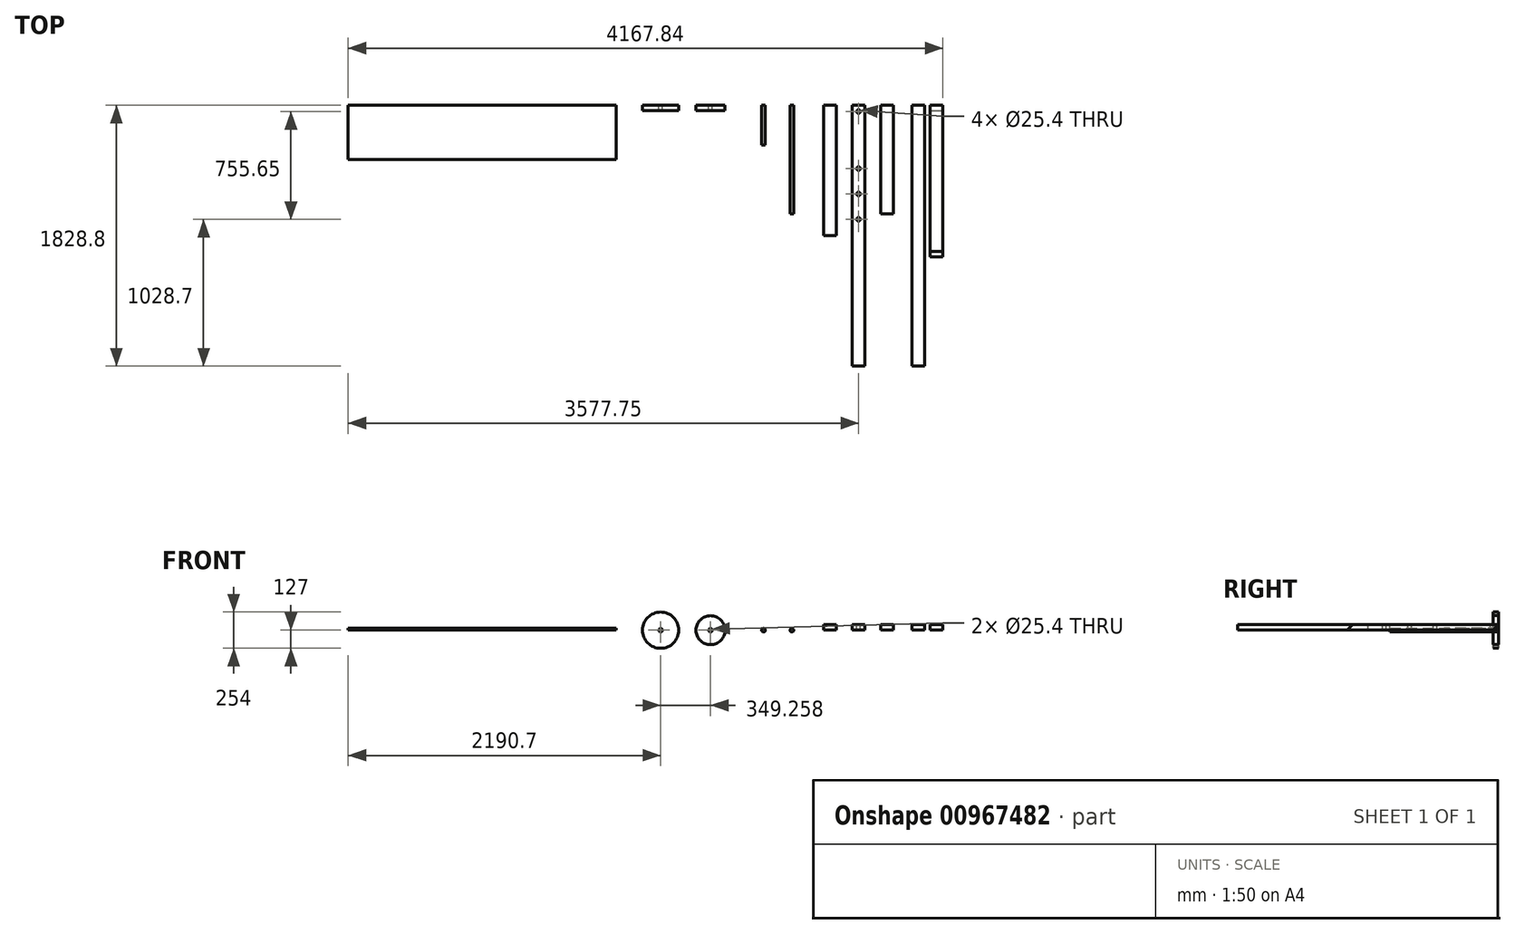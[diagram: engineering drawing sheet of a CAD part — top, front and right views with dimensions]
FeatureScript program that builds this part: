
annotation { "Feature Type Name" : "Feature", "Feature Type Description" : "" }
export const myFeature = defineFeature(function(context is Context, id is Id, definition is map)
    precondition{}
    {
        {
            var Q0;
            Q0=qCreatedBy(makeId("Front.planeOp"),FACE);
            var sketch = newSketch(context, id + "F0", { "sketchPlane" : qUnion([Q0])});
            skLineSegment(sketch, "E0.bottom", {"start": v(200.4, 0) * mm, "end": v(289.3, 0) * mm});
            skLineSegment(sketch, "E0.top", {"start": v(200.4, 38.1) * mm, "end": v(289.3, 38.1) * mm});
            skLineSegment(sketch, "E0.left", {"start": v(200.4, 0) * mm, "end": v(200.4, 38.1) * mm});
            skLineSegment(sketch, "E0.right", {"start": v(289.3, 0) * mm, "end": v(289.3, 38.1) * mm});
            skLineSegment(sketch, "E1.bottom", {"start": v(399.3, 0) * mm, "end": v(488.2, 0) * mm});
            skLineSegment(sketch, "E1.top", {"start": v(399.3, 38.1) * mm, "end": v(488.2, 38.1) * mm});
            skLineSegment(sketch, "E1.left", {"start": v(399.3, 0) * mm, "end": v(399.3, 38.1) * mm});
            skLineSegment(sketch, "E1.right", {"start": v(488.2, 0) * mm, "end": v(488.2, 38.1) * mm});
            skLineSegment(sketch, "E2.bottom", {"start": v(619.29, 0) * mm, "end": v(708.19, 0) * mm});
            skLineSegment(sketch, "E2.top", {"start": v(619.29, 38.1) * mm, "end": v(708.19, 38.1) * mm});
            skLineSegment(sketch, "E2.left", {"start": v(619.29, 0) * mm, "end": v(619.29, 38.1) * mm});
            skLineSegment(sketch, "E2.right", {"start": v(708.19, 0) * mm, "end": v(708.19, 38.1) * mm});
            skLineSegment(sketch, "E3.bottom", {"start": v(0, 0) * mm, "end": v(88.9, 0) * mm});
            skLineSegment(sketch, "E3.top", {"start": v(0, 38.1) * mm, "end": v(88.9, 38.1) * mm});
            skLineSegment(sketch, "E3.left", {"start": v(0, 0) * mm, "end": v(0, 38.1) * mm});
            skLineSegment(sketch, "E3.right", {"start": v(88.9, 0) * mm, "end": v(88.9, 38.1) * mm});
            skSolve(sketch);
        }
        {
            var Q0;
            Q0=makeQuery(id+"F0.imprint","IMPRINT",FACE,{"disambiguationData":[TD([[makeQuery(id+"F0.imprint","IMPRINT",EDGE,{"derivedFrom":sQuery(id+"F0.wireOp",EDGE,"E3.bottom")}),1.0]])]});
            extrude(context, id + "F1", {"entities" : qUnion([Q0]), "depth" : 914.4 * mm, "offsetDistance" : 25.4 * mm});
        }
        {
            var Q0;
            Q0=makeQuery(id+"F0.imprint","IMPRINT",FACE,{"disambiguationData":[TD([[makeQuery(id+"F0.imprint","IMPRINT",EDGE,{"derivedFrom":sQuery(id+"F0.wireOp",EDGE,"E0.bottom")}),1.0]])]});
            var Q1;
            Q1=makeQuery(id+"F0.imprint","IMPRINT",FACE,{"disambiguationData":[TD([[makeQuery(id+"F0.imprint","IMPRINT",EDGE,{"derivedFrom":sQuery(id+"F0.wireOp",EDGE,"E2.bottom")}),1.0]])]});
            extrude(context, id + "F2", {"entities" : qUnion([Q0, Q1]), "depth" : 1828.8 * mm, "offsetDistance" : 25.4 * mm});
        }
        {
            var Q0;
            Q0=makeQuery(id+"F0.imprint","IMPRINT",FACE,{"disambiguationData":[TD([[makeQuery(id+"F0.imprint","IMPRINT",EDGE,{"derivedFrom":sQuery(id+"F0.wireOp",EDGE,"E1.bottom")}),1.0]])]});
            extrude(context, id + "F3", {"entities" : qUnion([Q0]), "depth" : 762 * mm, "offsetDistance" : 25.4 * mm});
        }
        {
            var Q0;
            Q0=makeQuery(id+"F2.opExtrude","SWEPT_FACE",FACE,{"disambiguationData":[OSD([sQuery(id+"F0.wireOp",EDGE,"E0.top")])]});
            var sketch = newSketch(context, id + "F4", { "sketchPlane" : qUnion([Q0])});
            skCircle(sketch, "E4", {"center": v(244.85, -44.45) * mm, "radius": 12.7 * mm});
            skCircle(sketch, "E5", {"center": v(244.85, -622.3) * mm, "radius": 12.7 * mm});
            skLineSegment(sketch, "E6", {"start": v(200.4, -562.8) * mm, "end": v(200.4, -598.09) * mm});
            skLineSegment(sketch, "E7", {"start": v(289.3, -597.1) * mm, "end": v(289.3, -559.8) * mm});
            skCircle(sketch, "E8", {"center": v(244.85, -800.1) * mm, "radius": 12.7 * mm});
            skCircle(sketch, "E9", {"center": v(244.85, -444.5) * mm, "radius": 12.7 * mm});
            skSolve(sketch);
        }
        {
            var Q0;
            Q0=sQuery(id+"F4.wireOp",VERTEX,"E4.center");
            var Q1;
            Q1=sQuery(id+"F4.wireOp",VERTEX,"E9.center");
            var Q2;
            Q2=sQuery(id+"F4.wireOp",VERTEX,"E5.center");
            var Q3;
            Q3=sQuery(id+"F4.wireOp",VERTEX,"E8.center");
            var Q4;
            Q4=makeQuery(id+"F2.opExtrude","SWEPT_BODY",BODY,{"disambiguationData":[OSD([sQuery(id+"F0.wireOp",EDGE,"E0.bottom"),sQuery(id+"F0.wireOp",EDGE,"E0.top"),sQuery(id+"F0.wireOp",EDGE,"E0.left"),sQuery(id+"F0.wireOp",EDGE,"E0.right")])]});
            hole(context, id + "F5", {"style" : HoleStyle.SIMPLE, "endStyle" : HoleEndStyle.THROUGH, "holeDiameter" : 25.4 * mm, "majorDiameter" : 6.35 * mm, "isTappedThrough" : true, "tappedDepth" : 12.7 * mm, "tapClearance" : 3, "locations" : qUnion([Q0, Q1, Q2, Q3]), "scope" : qUnion([Q4])});
        }
        {
            var Q0;
            Q0=qCreatedBy(makeId("Top.planeOp"),FACE);
            var sketch = newSketch(context, id + "F6", { "sketchPlane" : qUnion([Q0])});
            skLineSegment(sketch, "E10.bottom", {"start": v(-1453.3, 0) * mm, "end": v(-3332.9, 0) * mm});
            skLineSegment(sketch, "E10.top", {"start": v(-1453.3, -381) * mm, "end": v(-3332.9, -381) * mm});
            skLineSegment(sketch, "E10.left", {"start": v(-1453.3, 0) * mm, "end": v(-1453.3, -381) * mm});
            skLineSegment(sketch, "E10.right", {"start": v(-3332.9, 0) * mm, "end": v(-3332.9, -381) * mm});
            skSolve(sketch);
        }
        {
            var Q0;
            Q0=makeQuery(id+"F6.imprint","IMPRINT",FACE,{"disambiguationData":[TD([[makeQuery(id+"F6.imprint","IMPRINT",EDGE,{"derivedFrom":sQuery(id+"F6.wireOp",EDGE,"E10.bottom")}),1.0]])]});
            extrude(context, id + "F7", {"entities" : qUnion([Q0]), "depth" : 12.7 * mm, "offsetDistance" : 25.4 * mm});
        }
        {
            var Q0;
            Q0=qCreatedBy(makeId("Front.planeOp"),FACE);
            var sketch = newSketch(context, id + "F8", { "sketchPlane" : qUnion([Q0])});
            skCircle(sketch, "E11", {"center": v(-222.22, 0) * mm, "radius": 12.7 * mm});
            skCircle(sketch, "E12", {"center": v(-421.27, 0) * mm, "radius": 12.7 * mm});
            skSolve(sketch);
        }
        {
            var Q0;
            Q0=makeQuery(id+"F8.imprint","IMPRINT",FACE,{"disambiguationData":[TD([[makeQuery(id+"F8.imprint","IMPRINT",EDGE,{"derivedFrom":sQuery(id+"F8.wireOp",EDGE,"E11")}),1.0]])]});
            extrude(context, id + "F9", {"entities" : qUnion([Q0]), "depth" : 762 * mm, "offsetDistance" : 25.4 * mm});
        }
        {
            var Q0;
            Q0=makeQuery(id+"F8.imprint","IMPRINT",FACE,{"disambiguationData":[TD([[makeQuery(id+"F8.imprint","IMPRINT",EDGE,{"derivedFrom":sQuery(id+"F8.wireOp",EDGE,"E12")}),1.0]])]});
            extrude(context, id + "F10", {"entities" : qUnion([Q0]), "depth" : 279.4 * mm, "offsetDistance" : 25.4 * mm});
        }
        {
            var Q0;
            Q0=qCreatedBy(makeId("Front.planeOp"),FACE);
            var sketch = newSketch(context, id + "F11", { "sketchPlane" : qUnion([Q0])});
            skCircle(sketch, "E13", {"center": v(-792.94, 0) * mm, "radius": 101.6 * mm});
            skCircle(sketch, "E14", {"center": v(-1142.2, 0) * mm, "radius": 127 * mm});
            skSolve(sketch);
        }
        {
            var Q0;
            Q0=makeQuery(id+"F11.imprint","IMPRINT",FACE,{"disambiguationData":[TD([[makeQuery(id+"F11.imprint","IMPRINT",EDGE,{"derivedFrom":sQuery(id+"F11.wireOp",EDGE,"E13")}),1.0]])]});
            extrude(context, id + "F12", {"entities" : qUnion([Q0]), "depth" : 38.1 * mm, "offsetDistance" : 25.4 * mm});
        }
        {
            var Q0;
            Q0=makeQuery(id+"F11.imprint","IMPRINT",FACE,{"disambiguationData":[TD([[makeQuery(id+"F11.imprint","IMPRINT",EDGE,{"derivedFrom":sQuery(id+"F11.wireOp",EDGE,"E14")}),1.0]])]});
            extrude(context, id + "F13", {"entities" : qUnion([Q0]), "depth" : 38.1 * mm, "offsetDistance" : 25.4 * mm});
        }
        {
            var Q0;
            Q0=sQuery(id+"F11.wireOp",VERTEX,"E13.center");
            var Q1;
            Q1=sQuery(id+"F11.wireOp",VERTEX,"E14.center");
            var Q2;
            Q2=makeQuery(id+"F12.opExtrude","SWEPT_BODY",BODY,{"disambiguationData":[OSD([sQuery(id+"F11.wireOp",EDGE,"E13")])]});
            hole(context, id + "F14", {"style" : HoleStyle.SIMPLE, "endStyle" : HoleEndStyle.THROUGH, "oppositeDirection" : true, "holeDiameter" : 25.4 * mm, "majorDiameter" : 6.35 * mm, "isTappedThrough" : true, "tappedDepth" : 12.7 * mm, "tapClearance" : 3, "locations" : qUnion([Q0, Q1]), "scope" : qUnion([Q2])});
        }
        {
            var Q0;
            Q0=sQuery(id+"F11.wireOp",VERTEX,"E14.center");
            var Q1;
            Q1=makeQuery(id+"F13.opExtrude","SWEPT_BODY",BODY,{"disambiguationData":[OSD([sQuery(id+"F11.wireOp",EDGE,"E14")])]});
            hole(context, id + "F15", {"style" : HoleStyle.SIMPLE, "endStyle" : HoleEndStyle.THROUGH, "oppositeDirection" : true, "holeDiameter" : 25.4 * mm, "majorDiameter" : 6.35 * mm, "isTappedThrough" : true, "tappedDepth" : 12.7 * mm, "tapClearance" : 3, "locations" : qUnion([Q0]), "scope" : qUnion([Q1])});
        }
        {
            var Q0;
            Q0=qCreatedBy(makeId("Front.planeOp"),FACE);
            var sketch = newSketch(context, id + "F16", { "sketchPlane" : qUnion([Q0])});
            skLineSegment(sketch, "E15.bottom", {"start": v(746.04, 0) * mm, "end": v(834.94, 0) * mm});
            skLineSegment(sketch, "E15.top", {"start": v(746.04, 38.1) * mm, "end": v(834.94, 38.1) * mm});
            skLineSegment(sketch, "E15.left", {"start": v(746.04, 0) * mm, "end": v(746.04, 38.1) * mm});
            skLineSegment(sketch, "E15.right", {"start": v(834.94, 0) * mm, "end": v(834.94, 38.1) * mm});
            skSolve(sketch);
        }
        {
            var Q0;
            Q0=makeQuery(id+"F16.imprint","IMPRINT",FACE,{"disambiguationData":[TD([[makeQuery(id+"F16.imprint","IMPRINT",EDGE,{"derivedFrom":sQuery(id+"F16.wireOp",EDGE,"E15.bottom")}),1.0]])]});
            extrude(context, id + "F17", {"entities" : qUnion([Q0]), "depth" : 1061.72 * mm, "offsetDistance" : 25.4 * mm});
        }
        {
            var Q0;
            Q0=makeQuery(id+"F17.opExtrude","CAP_EDGE",EDGE,{"disambiguationData":[OSD([sQuery(id+"F16.wireOp",EDGE,"E15.top")])],"isStart":false});
            var Q1;
            Q1=makeQuery(id+"F17.opExtrude","CAP_EDGE",EDGE,{"disambiguationData":[OSD([sQuery(id+"F16.wireOp",EDGE,"E15.bottom")])],"isStart":true});
            chamfer(context, id + "F18", {"entities" : qUnion([Q0, Q1]), "width" : 38.1 * mm, "tangentPropagation" : true});
        }
    });
